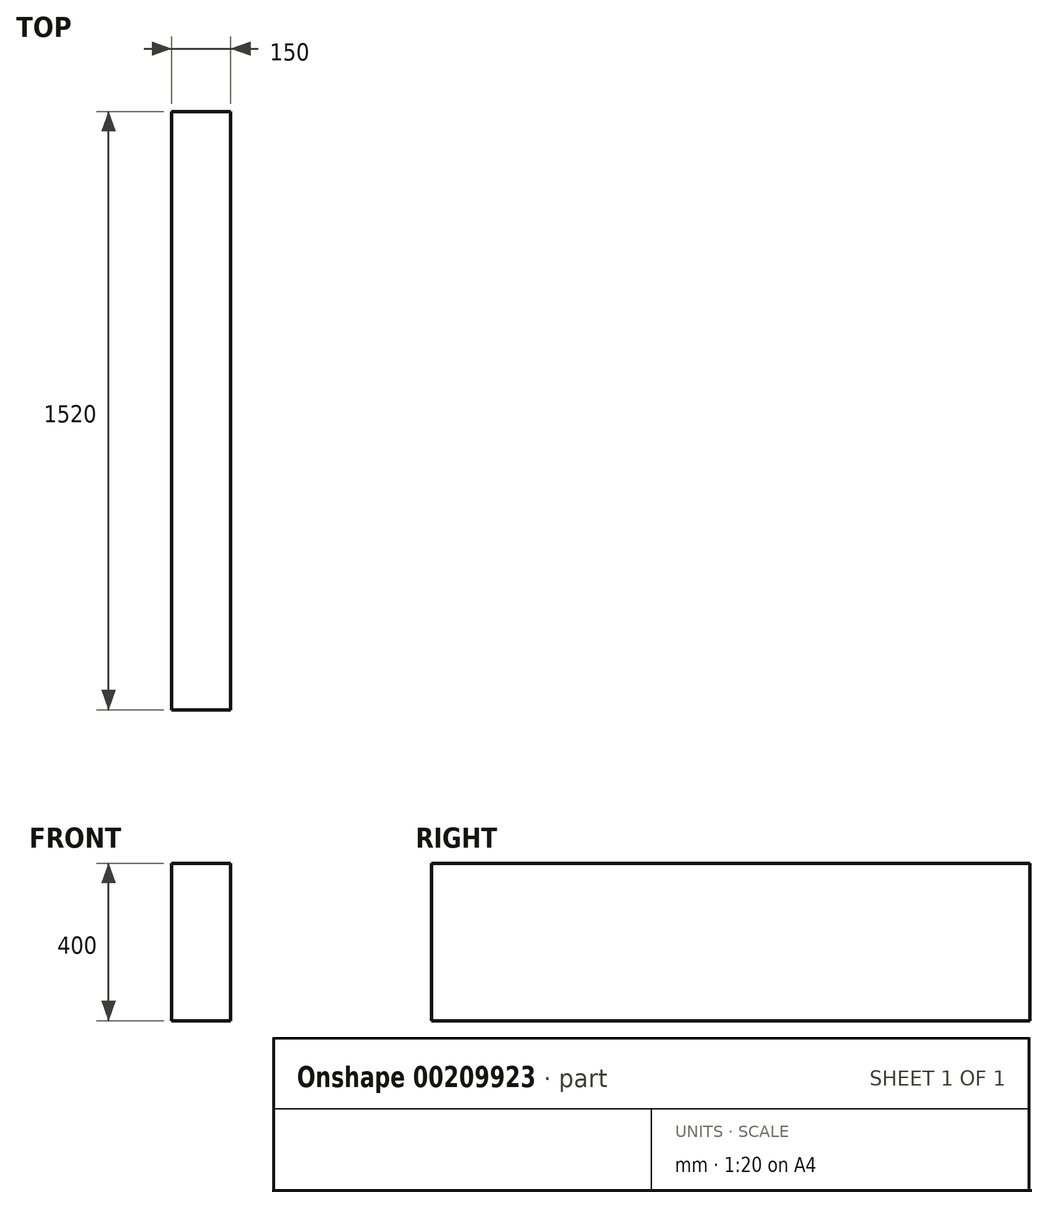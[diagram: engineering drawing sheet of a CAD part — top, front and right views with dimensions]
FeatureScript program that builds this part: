
annotation { "Feature Type Name" : "Feature", "Feature Type Description" : "" }
export const myFeature = defineFeature(function(context is Context, id is Id, definition is map)
    precondition{}
    {
        {
            var Q0;
            Q0=qCreatedBy(makeId("Top.planeOp"),FACE);
            var sketch = newSketch(context, id + "F0", { "sketchPlane" : qUnion([Q0])});
            skLineSegment(sketch, "E0.bottom", {"start": v(-79.63, 1520.71) * mm, "end": v(70.37, 1520.71) * mm});
            skLineSegment(sketch, "E0.top", {"start": v(-79.63, 0.71) * mm, "end": v(70.37, 0.71) * mm});
            skLineSegment(sketch, "E0.left", {"start": v(-79.63, 1520.71) * mm, "end": v(-79.63, 0.71) * mm});
            skLineSegment(sketch, "E0.right", {"start": v(70.37, 1520.71) * mm, "end": v(70.37, 0.71) * mm});
            skSolve(sketch);
        }
        {
            var Q0;
            Q0=makeQuery(id+"F0.imprint","IMPRINT",FACE,{"disambiguationData":[TD([[makeQuery(id+"F0.imprint","IMPRINT",EDGE,{"derivedFrom":sQuery(id+"F0.wireOp",EDGE,"E0.bottom")}),-1.0]])]});
            extrude(context, id + "F1", {"entities" : qUnion([Q0]), "depth" : 400 * mm});
        }
    });
